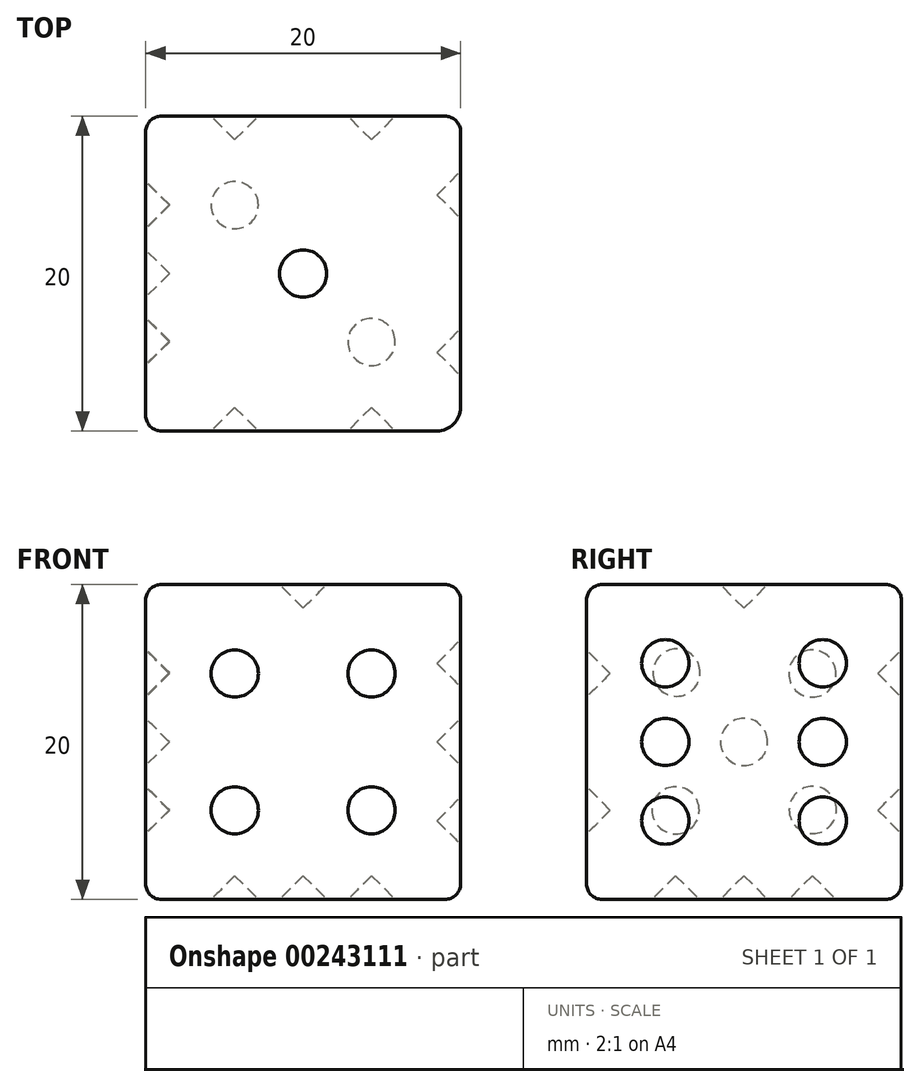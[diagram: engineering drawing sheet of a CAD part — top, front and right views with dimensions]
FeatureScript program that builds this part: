
annotation { "Feature Type Name" : "Feature", "Feature Type Description" : "" }
export const myFeature = defineFeature(function(context is Context, id is Id, definition is map)
    precondition{}
    {
        {
            var Q0;
            Q0=qCreatedBy(makeId("Top.planeOp"),FACE);
            var sketch = newSketch(context, id + "F0", { "sketchPlane" : qUnion([Q0])});
            skLineSegment(sketch, "E0.bottom", {"start": v(0, 0) * mm, "end": v(20, 0) * mm});
            skLineSegment(sketch, "E0.top", {"start": v(0, 20) * mm, "end": v(20, 20) * mm});
            skLineSegment(sketch, "E0.left", {"start": v(0, 0) * mm, "end": v(0, 20) * mm});
            skLineSegment(sketch, "E1", {"start": v(20, 20) * mm, "end": v(20, 0) * mm});
            skSolve(sketch);
        }
        {
            var Q0;
            Q0 = qSketchRegion(id + "F0", true);
            extrude(context, id + "F1", {"entities" : qUnion([Q0]), "depth" : 20 * mm});
        }
        {
            var Q0;
            Q0=makeQuery(id+"F1.opExtrude","CAP_FACE",FACE,{"disambiguationData":[OSD([sQuery(id+"F0.wireOp",EDGE,"E0.bottom"),sQuery(id+"F0.wireOp",EDGE,"E0.top"),sQuery(id+"F0.wireOp",EDGE,"E0.left"),sQuery(id+"F0.wireOp",EDGE,"E1")])],"isStart":false});
            var sketch = newSketch(context, id + "F2", { "sketchPlane" : qUnion([Q0])});
            skLineSegment(sketch, "E2", {"start": v(10, 20) * mm, "end": v(10, 0) * mm, "construction": true});
            skCircle(sketch, "E3", {"center": v(10, 10) * mm, "radius": 1.5 * mm});
            skSolve(sketch);
        }
        {
            var Q0;
            Q0=makeQuery(id+"F2.imprint","IMPRINT",FACE,{"disambiguationData":[TD([[makeQuery(id+"F2.imprint","IMPRINT",EDGE,{"derivedFrom":sQuery(id+"F2.wireOp",EDGE,"E3")}),1.0]])]});
            var Q1;
            Q1=sQuery(id+"F2.wireOp",EDGE,"E3");
            extrude(context, id + "F3", {"entities" : qUnion([Q0]), "operationType" : NewBodyOperationType.REMOVE, "surfaceEntities" : qUnion([Q1]), "oppositeDirection" : true, "depth" : 1.5 * mm});
        }
        {
            var Q0;
            Q0=makeQuery(id+"F1.opExtrude","SWEPT_FACE",FACE,{"disambiguationData":[OSD([sQuery(id+"F0.wireOp",EDGE,"E0.top")])]});
            var sketch = newSketch(context, id + "F4", { "sketchPlane" : qUnion([Q0])});
            skLineSegment(sketch, "E4", {"start": v(-20, 20) * mm, "end": v(-14.34, 14.34) * mm, "construction": true});
            skLineSegment(sketch, "E5", {"start": v(0, 0) * mm, "end": v(-5.66, 5.66) * mm, "construction": true});
            skCircle(sketch, "E6", {"center": v(-14.34, 14.34) * mm, "radius": 1.5 * mm});
            skCircle(sketch, "E7", {"center": v(-5.66, 5.66) * mm, "radius": 1.5 * mm});
            skSolve(sketch);
        }
        {
            var Q0;
            Q0 = qSketchRegion(id + "F4", true);
            extrude(context, id + "F5", {"entities" : qUnion([Q0]), "operationType" : NewBodyOperationType.REMOVE, "oppositeDirection" : true, "depth" : 1.5 * mm});
        }
        {
            var Q0;
            Q0=makeQuery(id+"F1.opExtrude","SWEPT_EDGE",EDGE,{"disambiguationData":[OSD([sQuery(id+"F0.wireOp",EDGE,"E0.bottom"),sQuery(id+"F0.wireOp",EDGE,"E0.left")])]});
            var Q1;
            Q1=makeQuery(id+"F1.opExtrude","CAP_EDGE",EDGE,{"disambiguationData":[OSD([sQuery(id+"F0.wireOp",EDGE,"E0.left")])],"isStart":true});
            var Q2;
            Q2=makeQuery(id+"F1.opExtrude","SWEPT_EDGE",EDGE,{"disambiguationData":[OSD([sQuery(id+"F0.wireOp",EDGE,"E0.top"),sQuery(id+"F0.wireOp",EDGE,"E1")])]});
            var Q3;
            Q3=makeQuery(id+"F1.opExtrude","SWEPT_EDGE",EDGE,{"disambiguationData":[OSD([sQuery(id+"F0.wireOp",EDGE,"E0.top"),sQuery(id+"F0.wireOp",EDGE,"E0.left")])]});
            var Q4;
            Q4=makeQuery(id+"F1.opExtrude","CAP_EDGE",EDGE,{"disambiguationData":[OSD([sQuery(id+"F0.wireOp",EDGE,"E0.top")])],"isStart":false});
            var Q5;
            Q5=makeQuery(id+"F1.opExtrude","CAP_EDGE",EDGE,{"disambiguationData":[OSD([sQuery(id+"F0.wireOp",EDGE,"E0.left")])],"isStart":false});
            var Q6;
            Q6=makeQuery(id+"F1.opExtrude","CAP_EDGE",EDGE,{"disambiguationData":[OSD([sQuery(id+"F0.wireOp",EDGE,"E0.bottom")])],"isStart":true});
            var Q7;
            Q7=makeQuery(id+"F1.opExtrude","CAP_EDGE",EDGE,{"disambiguationData":[OSD([sQuery(id+"F0.wireOp",EDGE,"E1")])],"isStart":true});
            var Q8;
            Q8=makeQuery(id+"F1.opExtrude","CAP_EDGE",EDGE,{"disambiguationData":[OSD([sQuery(id+"F0.wireOp",EDGE,"E1")])],"isStart":false});
            var Q9;
            Q9=makeQuery(id+"F1.opExtrude","CAP_EDGE",EDGE,{"disambiguationData":[OSD([sQuery(id+"F0.wireOp",EDGE,"E0.bottom")])],"isStart":false});
            var Q10;
            Q10=makeQuery(id+"F1.opExtrude","CAP_EDGE",EDGE,{"disambiguationData":[OSD([sQuery(id+"F0.wireOp",EDGE,"E0.top")])],"isStart":true});
            fillet(context, id + "F6", {"entities" : qUnion([Q0, Q1, Q2, Q3, Q4, Q5, Q6, Q7, Q8, Q9, Q10]), "radius" : 1 * mm, "tangentPropagation" : true, "allowEdgeOverflow" : false});
        }
        {
            var Q0;
            Q0=makeQuery(id+"F5.boolean.opBoolean","COPY",EDGE,{"derivedFrom":makeQuery(id+"F5.opExtrude","CAP_EDGE",EDGE,{"disambiguationData":[OSD([sQuery(id+"F4.wireOp",EDGE,"E7")])],"isStart":false})});
            chamfer(context, id + "F7", {"entities" : qUnion([Q0]), "width" : 1.5 * mm, "tangentPropagation" : true});
        }
        {
            var Q0;
            Q0=makeQuery(id+"F1.opExtrude","CAP_FACE",FACE,{"disambiguationData":[OSD([sQuery(id+"F0.wireOp",EDGE,"E0.bottom"),sQuery(id+"F0.wireOp",EDGE,"E0.top"),sQuery(id+"F0.wireOp",EDGE,"E0.left"),sQuery(id+"F0.wireOp",EDGE,"E1")])],"isStart":true});
            var sketch = newSketch(context, id + "F8", { "sketchPlane" : qUnion([Q0])});
            skCircle(sketch, "E8", {"center": v(5.66, -14.34) * mm, "radius": 1.5 * mm});
            skCircle(sketch, "E9", {"center": v(14.34, -5.66) * mm, "radius": 1.5 * mm});
            skCircle(sketch, "E10", {"center": v(10, -10) * mm, "radius": 1.5 * mm});
            skSolve(sketch);
        }
        {
            var Q0;
            Q0=makeQuery(id+"F8.imprint","IMPRINT",FACE,{"disambiguationData":[TD([[makeQuery(id+"F8.imprint","IMPRINT",EDGE,{"derivedFrom":sQuery(id+"F8.wireOp",EDGE,"E8")}),1.0]])]});
            var Q1;
            Q1=makeQuery(id+"F8.imprint","IMPRINT",FACE,{"disambiguationData":[TD([[makeQuery(id+"F8.imprint","IMPRINT",EDGE,{"derivedFrom":sQuery(id+"F8.wireOp",EDGE,"E10")}),1.0]])]});
            var Q2;
            Q2=makeQuery(id+"F8.imprint","IMPRINT",FACE,{"disambiguationData":[TD([[makeQuery(id+"F8.imprint","IMPRINT",EDGE,{"derivedFrom":sQuery(id+"F8.wireOp",EDGE,"E9")}),1.0]])]});
            extrude(context, id + "F9", {"entities" : qUnion([Q0, Q1, Q2]), "operationType" : NewBodyOperationType.REMOVE, "oppositeDirection" : true, "depth" : 1.5 * mm});
        }
        {
            var Q0;
            Q0=makeQuery(id+"F5.boolean.opBoolean","COPY",FACE,{"derivedFrom":makeQuery(id+"F5.opExtrude","CAP_FACE",FACE,{"disambiguationData":[OSD([sQuery(id+"F4.wireOp",EDGE,"E6")])],"isStart":false})});
            chamfer(context, id + "F10", {"entities" : qUnion([Q0]), "width" : 1.5 * mm, "tangentPropagation" : true});
        }
        {
            var Q0;
            Q0=makeQuery(id+"F3.boolean.opBoolean","COPY",EDGE,{"derivedFrom":makeQuery(id+"F3.opExtrude","CAP_EDGE",EDGE,{"disambiguationData":[OSD([sQuery(id+"F2.wireOp",EDGE,"E3")])],"isStart":false})});
            chamfer(context, id + "F11", {"entities" : qUnion([Q0]), "width" : 1.5 * mm, "tangentPropagation" : true});
        }
        {
            var Q0;
            Q0=makeQuery(id+"F1.opExtrude","SWEPT_EDGE",EDGE,{"disambiguationData":[OSD([sQuery(id+"F0.wireOp",EDGE,"E0.bottom"),sQuery(id+"F0.wireOp",EDGE,"E1")])]});
            fillet(context, id + "F12", {"entities" : qUnion([Q0]), "radius" : 1.5 * mm, "tangentPropagation" : true, "allowEdgeOverflow" : false});
        }
        {
            var Q0;
            Q0=makeQuery(id+"F9.boolean.opBoolean","COPY",EDGE,{"derivedFrom":makeQuery(id+"F9.opExtrude","CAP_EDGE",EDGE,{"disambiguationData":[OSD([sQuery(id+"F8.wireOp",EDGE,"E8")])],"isStart":false})});
            var Q1;
            Q1=makeQuery(id+"F9.boolean.opBoolean","COPY",EDGE,{"derivedFrom":makeQuery(id+"F9.opExtrude","CAP_EDGE",EDGE,{"disambiguationData":[OSD([sQuery(id+"F8.wireOp",EDGE,"E10")])],"isStart":false})});
            var Q2;
            Q2=makeQuery(id+"F9.boolean.opBoolean","COPY",EDGE,{"derivedFrom":makeQuery(id+"F9.opExtrude","CAP_EDGE",EDGE,{"disambiguationData":[OSD([sQuery(id+"F8.wireOp",EDGE,"E9")])],"isStart":false})});
            chamfer(context, id + "F13", {"entities" : qUnion([Q0, Q1, Q2]), "width" : 1.5 * mm, "tangentPropagation" : true});
        }
        {
            var Q0;
            Q0=makeQuery(id+"F1.opExtrude","SWEPT_FACE",FACE,{"disambiguationData":[OSD([sQuery(id+"F0.wireOp",EDGE,"E0.bottom")])]});
            var sketch = newSketch(context, id + "F14", { "sketchPlane" : qUnion([Q0])});
            skCircle(sketch, "E11", {"center": v(5.66, 14.34) * mm, "radius": 1.5 * mm});
            skCircle(sketch, "E12", {"center": v(14.34, 5.66) * mm, "radius": 1.5 * mm});
            skCircle(sketch, "E13", {"center": v(5.66, 5.66) * mm, "radius": 1.5 * mm});
            skCircle(sketch, "E14", {"center": v(14.34, 14.34) * mm, "radius": 1.5 * mm});
            skSolve(sketch);
        }
        {
            var Q0;
            Q0=makeQuery(id+"F14.imprint","IMPRINT",FACE,{"disambiguationData":[TD([[makeQuery(id+"F14.imprint","IMPRINT",EDGE,{"derivedFrom":sQuery(id+"F14.wireOp",EDGE,"E13")}),1.0]])]});
            var Q1;
            Q1=makeQuery(id+"F14.imprint","IMPRINT",FACE,{"disambiguationData":[TD([[makeQuery(id+"F14.imprint","IMPRINT",EDGE,{"derivedFrom":sQuery(id+"F14.wireOp",EDGE,"E11")}),1.0]])]});
            var Q2;
            Q2=makeQuery(id+"F14.imprint","IMPRINT",FACE,{"disambiguationData":[TD([[makeQuery(id+"F14.imprint","IMPRINT",EDGE,{"derivedFrom":sQuery(id+"F14.wireOp",EDGE,"E14")}),1.0]])]});
            var Q3;
            Q3=makeQuery(id+"F14.imprint","IMPRINT",FACE,{"disambiguationData":[TD([[makeQuery(id+"F14.imprint","IMPRINT",EDGE,{"derivedFrom":sQuery(id+"F14.wireOp",EDGE,"E12")}),1.0]])]});
            extrude(context, id + "F15", {"entities" : qUnion([Q0, Q1, Q2, Q3]), "operationType" : NewBodyOperationType.REMOVE, "oppositeDirection" : true, "depth" : 1.5 * mm});
        }
        {
            var Q0;
            Q0=makeQuery(id+"F15.boolean.opBoolean","COPY",EDGE,{"derivedFrom":makeQuery(id+"F15.opExtrude","CAP_EDGE",EDGE,{"disambiguationData":[OSD([sQuery(id+"F14.wireOp",EDGE,"E11")])],"isStart":false})});
            var Q1;
            Q1=makeQuery(id+"F15.boolean.opBoolean","COPY",EDGE,{"derivedFrom":makeQuery(id+"F15.opExtrude","CAP_EDGE",EDGE,{"disambiguationData":[OSD([sQuery(id+"F14.wireOp",EDGE,"E14")])],"isStart":false})});
            var Q2;
            Q2=makeQuery(id+"F15.boolean.opBoolean","COPY",EDGE,{"derivedFrom":makeQuery(id+"F15.opExtrude","CAP_EDGE",EDGE,{"disambiguationData":[OSD([sQuery(id+"F14.wireOp",EDGE,"E13")])],"isStart":false})});
            var Q3;
            Q3=makeQuery(id+"F15.boolean.opBoolean","COPY",EDGE,{"derivedFrom":makeQuery(id+"F15.opExtrude","CAP_EDGE",EDGE,{"disambiguationData":[OSD([sQuery(id+"F14.wireOp",EDGE,"E12")])],"isStart":false})});
            chamfer(context, id + "F16", {"entities" : qUnion([Q0, Q1, Q2, Q3]), "width" : 1.5 * mm, "tangentPropagation" : true});
        }
        {
            var Q0;
            Q0=makeQuery(id+"F1.opExtrude","SWEPT_FACE",FACE,{"disambiguationData":[OSD([sQuery(id+"F0.wireOp",EDGE,"E0.left")])]});
            var sketch = newSketch(context, id + "F17", { "sketchPlane" : qUnion([Q0])});
            skCircle(sketch, "E15", {"center": v(-14.34, 14.34) * mm, "radius": 1.5 * mm});
            skCircle(sketch, "E16", {"center": v(-14.37, 5.68) * mm, "radius": 1.5 * mm});
            skCircle(sketch, "E17", {"center": v(-5.71, 14.4) * mm, "radius": 1.5 * mm});
            skCircle(sketch, "E18", {"center": v(-5.66, 5.66) * mm, "radius": 1.5 * mm});
            skCircle(sketch, "E19", {"center": v(-10, 10) * mm, "radius": 1.5 * mm});
            skSolve(sketch);
        }
        {
            var Q0;
            Q0=makeQuery(id+"F17.imprint","IMPRINT",FACE,{"disambiguationData":[TD([[makeQuery(id+"F17.imprint","IMPRINT",EDGE,{"derivedFrom":sQuery(id+"F17.wireOp",EDGE,"E15")}),1.0]])]});
            var Q1;
            Q1=makeQuery(id+"F17.imprint","IMPRINT",FACE,{"disambiguationData":[TD([[makeQuery(id+"F17.imprint","IMPRINT",EDGE,{"derivedFrom":sQuery(id+"F17.wireOp",EDGE,"E17")}),1.0]])]});
            var Q2;
            Q2=makeQuery(id+"F17.imprint","IMPRINT",FACE,{"disambiguationData":[TD([[makeQuery(id+"F17.imprint","IMPRINT",EDGE,{"derivedFrom":sQuery(id+"F17.wireOp",EDGE,"E19")}),1.0]])]});
            var Q3;
            Q3=makeQuery(id+"F17.imprint","IMPRINT",FACE,{"disambiguationData":[TD([[makeQuery(id+"F17.imprint","IMPRINT",EDGE,{"derivedFrom":sQuery(id+"F17.wireOp",EDGE,"E16")}),1.0]])]});
            var Q4;
            Q4=makeQuery(id+"F17.imprint","IMPRINT",FACE,{"disambiguationData":[TD([[makeQuery(id+"F17.imprint","IMPRINT",EDGE,{"derivedFrom":sQuery(id+"F17.wireOp",EDGE,"E18")}),1.0]])]});
            extrude(context, id + "F18", {"entities" : qUnion([Q0, Q1, Q2, Q3, Q4]), "operationType" : NewBodyOperationType.REMOVE, "oppositeDirection" : true, "depth" : 1.5 * mm});
        }
        {
            var Q0;
            Q0=makeQuery(id+"F18.boolean.opBoolean","COPY",EDGE,{"derivedFrom":makeQuery(id+"F18.opExtrude","CAP_EDGE",EDGE,{"disambiguationData":[OSD([sQuery(id+"F17.wireOp",EDGE,"E15")])],"isStart":false})});
            var Q1;
            Q1=makeQuery(id+"F18.boolean.opBoolean","COPY",EDGE,{"derivedFrom":makeQuery(id+"F18.opExtrude","CAP_EDGE",EDGE,{"disambiguationData":[OSD([sQuery(id+"F17.wireOp",EDGE,"E16")])],"isStart":false})});
            var Q2;
            Q2=makeQuery(id+"F18.boolean.opBoolean","COPY",EDGE,{"derivedFrom":makeQuery(id+"F18.opExtrude","CAP_EDGE",EDGE,{"disambiguationData":[OSD([sQuery(id+"F17.wireOp",EDGE,"E19")])],"isStart":false})});
            var Q3;
            Q3=makeQuery(id+"F18.boolean.opBoolean","COPY",EDGE,{"derivedFrom":makeQuery(id+"F18.opExtrude","CAP_EDGE",EDGE,{"disambiguationData":[OSD([sQuery(id+"F17.wireOp",EDGE,"E17")])],"isStart":false})});
            var Q4;
            Q4=makeQuery(id+"F18.boolean.opBoolean","COPY",EDGE,{"derivedFrom":makeQuery(id+"F18.opExtrude","CAP_EDGE",EDGE,{"disambiguationData":[OSD([sQuery(id+"F17.wireOp",EDGE,"E18")])],"isStart":false})});
            chamfer(context, id + "F19", {"entities" : qUnion([Q0, Q1, Q2, Q3, Q4]), "width" : 1.5 * mm, "tangentPropagation" : true});
        }
        {
            var Q0;
            Q0=makeQuery(id+"F1.opExtrude","SWEPT_FACE",FACE,{"disambiguationData":[OSD([sQuery(id+"F0.wireOp",EDGE,"E1")])]});
            var sketch = newSketch(context, id + "F20", { "sketchPlane" : qUnion([Q0])});
            skCircle(sketch, "E20", {"center": v(5, 15) * mm, "radius": 1.5 * mm});
            skCircle(sketch, "E21", {"center": v(15, 15) * mm, "radius": 1.5 * mm});
            skCircle(sketch, "E22", {"center": v(5, 10) * mm, "radius": 1.5 * mm});
            skCircle(sketch, "E23", {"center": v(15, 10) * mm, "radius": 1.5 * mm});
            skCircle(sketch, "E24", {"center": v(5, 5) * mm, "radius": 1.5 * mm});
            skCircle(sketch, "E25", {"center": v(15, 5) * mm, "radius": 1.5 * mm});
            skSolve(sketch);
        }
        {
            var Q0;
            Q0=makeQuery(id+"F20.imprint","IMPRINT",FACE,{"disambiguationData":[TD([[makeQuery(id+"F20.imprint","IMPRINT",EDGE,{"derivedFrom":sQuery(id+"F20.wireOp",EDGE,"E21")}),1.0]])]});
            var Q1;
            Q1=makeQuery(id+"F20.imprint","IMPRINT",FACE,{"disambiguationData":[TD([[makeQuery(id+"F20.imprint","IMPRINT",EDGE,{"derivedFrom":sQuery(id+"F20.wireOp",EDGE,"E20")}),1.0]])]});
            var Q2;
            Q2=makeQuery(id+"F20.imprint","IMPRINT",FACE,{"disambiguationData":[TD([[makeQuery(id+"F20.imprint","IMPRINT",EDGE,{"derivedFrom":sQuery(id+"F20.wireOp",EDGE,"E22")}),1.0]])]});
            var Q3;
            Q3=makeQuery(id+"F20.imprint","IMPRINT",FACE,{"disambiguationData":[TD([[makeQuery(id+"F20.imprint","IMPRINT",EDGE,{"derivedFrom":sQuery(id+"F20.wireOp",EDGE,"E23")}),1.0]])]});
            var Q4;
            Q4=makeQuery(id+"F20.imprint","IMPRINT",FACE,{"disambiguationData":[TD([[makeQuery(id+"F20.imprint","IMPRINT",EDGE,{"derivedFrom":sQuery(id+"F20.wireOp",EDGE,"E25")}),1.0]])]});
            var Q5;
            Q5=makeQuery(id+"F20.imprint","IMPRINT",FACE,{"disambiguationData":[TD([[makeQuery(id+"F20.imprint","IMPRINT",EDGE,{"derivedFrom":sQuery(id+"F20.wireOp",EDGE,"E24")}),1.0]])]});
            extrude(context, id + "F21", {"entities" : qUnion([Q0, Q1, Q2, Q3, Q4, Q5]), "operationType" : NewBodyOperationType.REMOVE, "oppositeDirection" : true, "depth" : 1.5 * mm});
        }
        {
            var Q0;
            Q0=makeQuery(id+"F21.boolean.opBoolean","COPY",EDGE,{"derivedFrom":makeQuery(id+"F21.opExtrude","CAP_EDGE",EDGE,{"disambiguationData":[OSD([sQuery(id+"F20.wireOp",EDGE,"E25")])],"isStart":false})});
            var Q1;
            Q1=makeQuery(id+"F21.boolean.opBoolean","COPY",EDGE,{"derivedFrom":makeQuery(id+"F21.opExtrude","CAP_EDGE",EDGE,{"disambiguationData":[OSD([sQuery(id+"F20.wireOp",EDGE,"E23")])],"isStart":false})});
            var Q2;
            Q2=makeQuery(id+"F21.boolean.opBoolean","COPY",EDGE,{"derivedFrom":makeQuery(id+"F21.opExtrude","CAP_EDGE",EDGE,{"disambiguationData":[OSD([sQuery(id+"F20.wireOp",EDGE,"E22")])],"isStart":false})});
            var Q3;
            Q3=makeQuery(id+"F21.boolean.opBoolean","COPY",EDGE,{"derivedFrom":makeQuery(id+"F21.opExtrude","CAP_EDGE",EDGE,{"disambiguationData":[OSD([sQuery(id+"F20.wireOp",EDGE,"E24")])],"isStart":false})});
            var Q4;
            Q4=makeQuery(id+"F21.boolean.opBoolean","COPY",EDGE,{"derivedFrom":makeQuery(id+"F21.opExtrude","CAP_EDGE",EDGE,{"disambiguationData":[OSD([sQuery(id+"F20.wireOp",EDGE,"E20")])],"isStart":false})});
            var Q5;
            Q5=makeQuery(id+"F21.boolean.opBoolean","COPY",EDGE,{"derivedFrom":makeQuery(id+"F21.opExtrude","CAP_EDGE",EDGE,{"disambiguationData":[OSD([sQuery(id+"F20.wireOp",EDGE,"E21")])],"isStart":false})});
            chamfer(context, id + "F22", {"entities" : qUnion([Q0, Q1, Q2, Q3, Q4, Q5]), "width" : 1.5 * mm, "tangentPropagation" : true});
        }
    });
